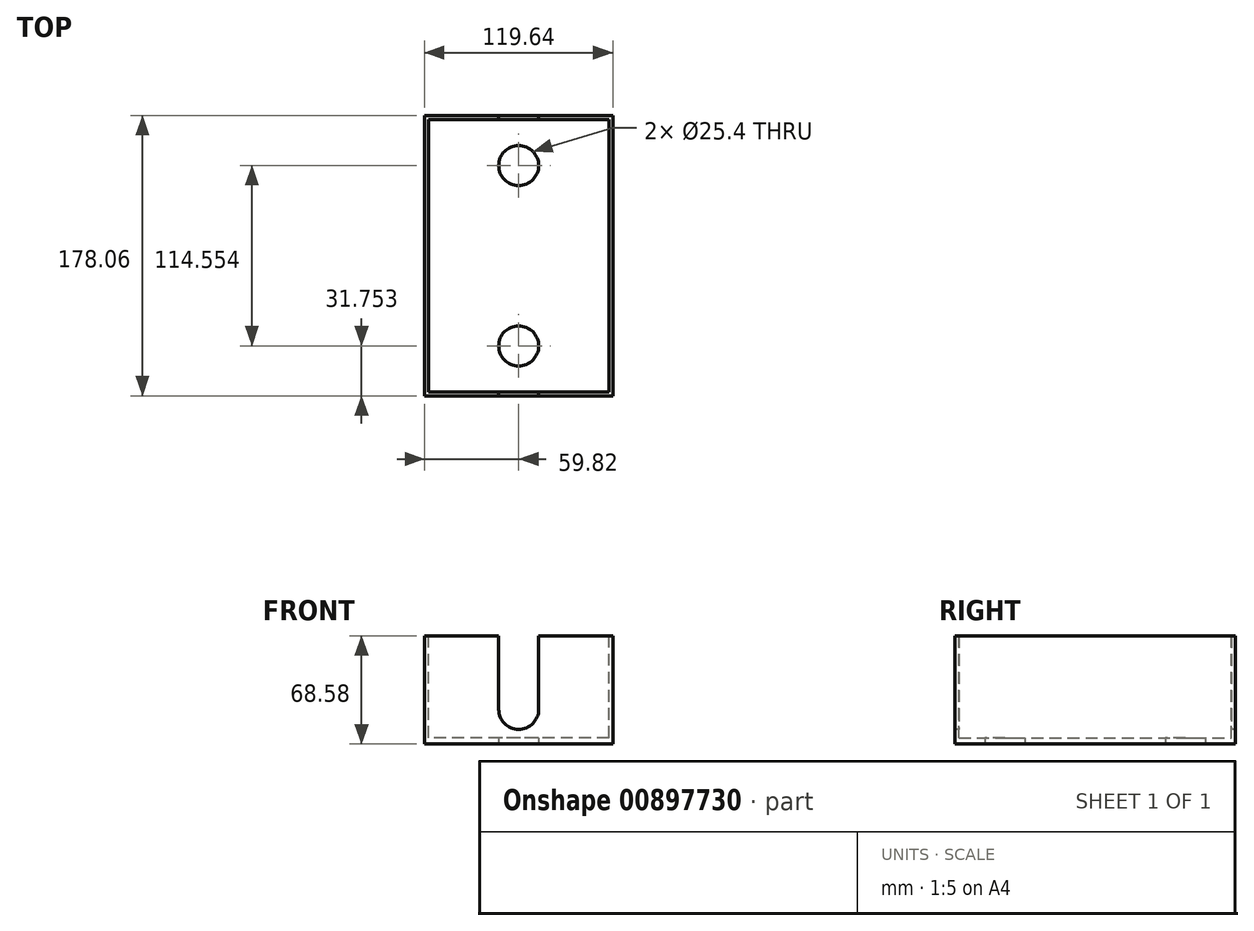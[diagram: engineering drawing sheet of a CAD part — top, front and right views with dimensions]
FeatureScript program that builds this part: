
annotation { "Feature Type Name" : "Feature", "Feature Type Description" : "" }
export const myFeature = defineFeature(function(context is Context, id is Id, definition is map)
    precondition{}
    {
        {
            var Q0;
            Q0=qCreatedBy(makeId("Top.planeOp"),FACE);
            var sketch = newSketch(context, id + "F0", { "sketchPlane" : qUnion([Q0])});
            skLineSegment(sketch, "E0.bottom", {"start": v(59.82, -89.03) * mm, "end": v(-59.82, -89.03) * mm});
            skLineSegment(sketch, "E0.top", {"start": v(59.82, 89.03) * mm, "end": v(-59.82, 89.03) * mm});
            skLineSegment(sketch, "E0.left", {"start": v(59.82, -89.03) * mm, "end": v(59.82, 89.03) * mm});
            skLineSegment(sketch, "E0.right", {"start": v(-59.82, -89.03) * mm, "end": v(-59.82, 89.03) * mm});
            skPoint(sketch, "E0.middle", {"position": v(0, 0) * mm});
            skSolve(sketch);
        }
        {
            var Q0;
            Q0=makeQuery(id+"F0.imprint","IMPRINT",FACE,{"disambiguationData":[TD([[makeQuery(id+"F0.imprint","IMPRINT",EDGE,{"derivedFrom":sQuery(id+"F0.wireOp",EDGE,"E0.bottom")}),-1.0]])]});
            extrude(context, id + "F1", {"entities" : qUnion([Q0]), "depth" : 68.58 * mm, "offsetDistance" : 25.4 * mm});
        }
        {
            var Q0;
            Q0=makeQuery(id+"F1.opExtrude","CAP_FACE",FACE,{"disambiguationData":[OSD([sQuery(id+"F0.wireOp",EDGE,"E0.bottom"),sQuery(id+"F0.wireOp",EDGE,"E0.top"),sQuery(id+"F0.wireOp",EDGE,"E0.left"),sQuery(id+"F0.wireOp",EDGE,"E0.right")])],"isStart":false});
            var sketch = newSketch(context, id + "F2", { "sketchPlane" : qUnion([Q0])});
            skLineSegment(sketch, "E1.bottom", {"start": v(57.28, -86.49) * mm, "end": v(-57.28, -86.49) * mm});
            skLineSegment(sketch, "E1.top", {"start": v(57.28, 86.49) * mm, "end": v(-57.28, 86.49) * mm});
            skLineSegment(sketch, "E1.left", {"start": v(57.28, -86.49) * mm, "end": v(57.28, 86.49) * mm});
            skLineSegment(sketch, "E1.right", {"start": v(-57.28, -86.49) * mm, "end": v(-57.28, 86.49) * mm});
            skPoint(sketch, "E1.middle", {"position": v(0, 0) * mm});
            skSolve(sketch);
        }
        {
            var Q0;
            Q0=makeQuery(id+"F2.imprint","IMPRINT",FACE,{"disambiguationData":[TD([[makeQuery(id+"F2.imprint","IMPRINT",EDGE,{"derivedFrom":sQuery(id+"F2.wireOp",EDGE,"E1.bottom")}),-1.0]])]});
            extrude(context, id + "F3", {"entities" : qUnion([Q0]), "operationType" : NewBodyOperationType.REMOVE, "oppositeDirection" : true, "depth" : 64.77 * mm, "offsetDistance" : 25.4 * mm});
        }
        {
            var Q0;
            Q0=makeQuery(id+"F1.opExtrude","SWEPT_FACE",FACE,{"disambiguationData":[OSD([sQuery(id+"F0.wireOp",EDGE,"E0.bottom")])]});
            var sketch = newSketch(context, id + "F4", { "sketchPlane" : qUnion([Q0])});
            skCircle(sketch, "E2", {"center": v(0, 21.97) * mm, "radius": 12.7 * mm});
            skLineSegment(sketch, "E3", {"start": v(12.7, 21.97) * mm, "end": v(12.7, 68.58) * mm});
            skLineSegment(sketch, "E4", {"start": v(-12.7, 21.97) * mm, "end": v(-12.7, 68.58) * mm});
            skLineSegment(sketch, "E5", {"start": v(-12.7, 68.58) * mm, "end": v(12.7, 68.58) * mm});
            skSolve(sketch);
        }
        {
            var Q0;
            {var subQ0=sQuery(id+"F4.wireOp",EDGE,"E2");var subQ1=makeQuery(id+"F4.imprint","INTERSECT",VERTEX,{"derivedFrom":[subQ0,sQuery(id+"F4.wireOp",EDGE,"E3")]});Q0=makeQuery(id+"F4.imprint","IMPRINT",FACE,{"disambiguationData":[TD([[makeQuery(id+"F4.imprint","IMPRINT",EDGE,{"disambiguationData":[TD([[subQ1,-1.0]])],"derivedFrom":subQ0}),1.0]])]});}
            var Q1;
            {var subQ0=sQuery(id+"F4.wireOp",EDGE,"E3");Q1=makeQuery(id+"F4.imprint","IMPRINT",FACE,{"disambiguationData":[TD([[makeQuery(id+"F4.imprint","IMPRINT",EDGE,{"derivedFrom":subQ0}),1.0]])]});}
            extrude(context, id + "F5", {"entities" : qUnion([Q0, Q1]), "operationType" : NewBodyOperationType.REMOVE, "oppositeDirection" : true, "depth" : 190.5 * mm, "offsetDistance" : 25.4 * mm});
        }
        {
            var Q0;
            Q0=makeQuery(id+"F1.opExtrude","CAP_FACE",FACE,{"disambiguationData":[OSD([sQuery(id+"F0.wireOp",EDGE,"E0.bottom"),sQuery(id+"F0.wireOp",EDGE,"E0.top"),sQuery(id+"F0.wireOp",EDGE,"E0.left"),sQuery(id+"F0.wireOp",EDGE,"E0.right")])],"isStart":true});
            var sketch = newSketch(context, id + "F6", { "sketchPlane" : qUnion([Q0])});
            skCircle(sketch, "E6", {"center": v(0, 57.28) * mm, "radius": 12.7 * mm});
            skCircle(sketch, "E7", {"center": v(0, -57.28) * mm, "radius": 12.7 * mm});
            skSolve(sketch);
        }
        {
            var Q0;
            Q0 = qSketchRegion(id + "F6", true);
            extrude(context, id + "F7", {"entities" : qUnion([Q0]), "operationType" : NewBodyOperationType.REMOVE, "oppositeDirection" : true, "depth" : 5.08 * mm, "offsetDistance" : 25.4 * mm});
        }
    });
